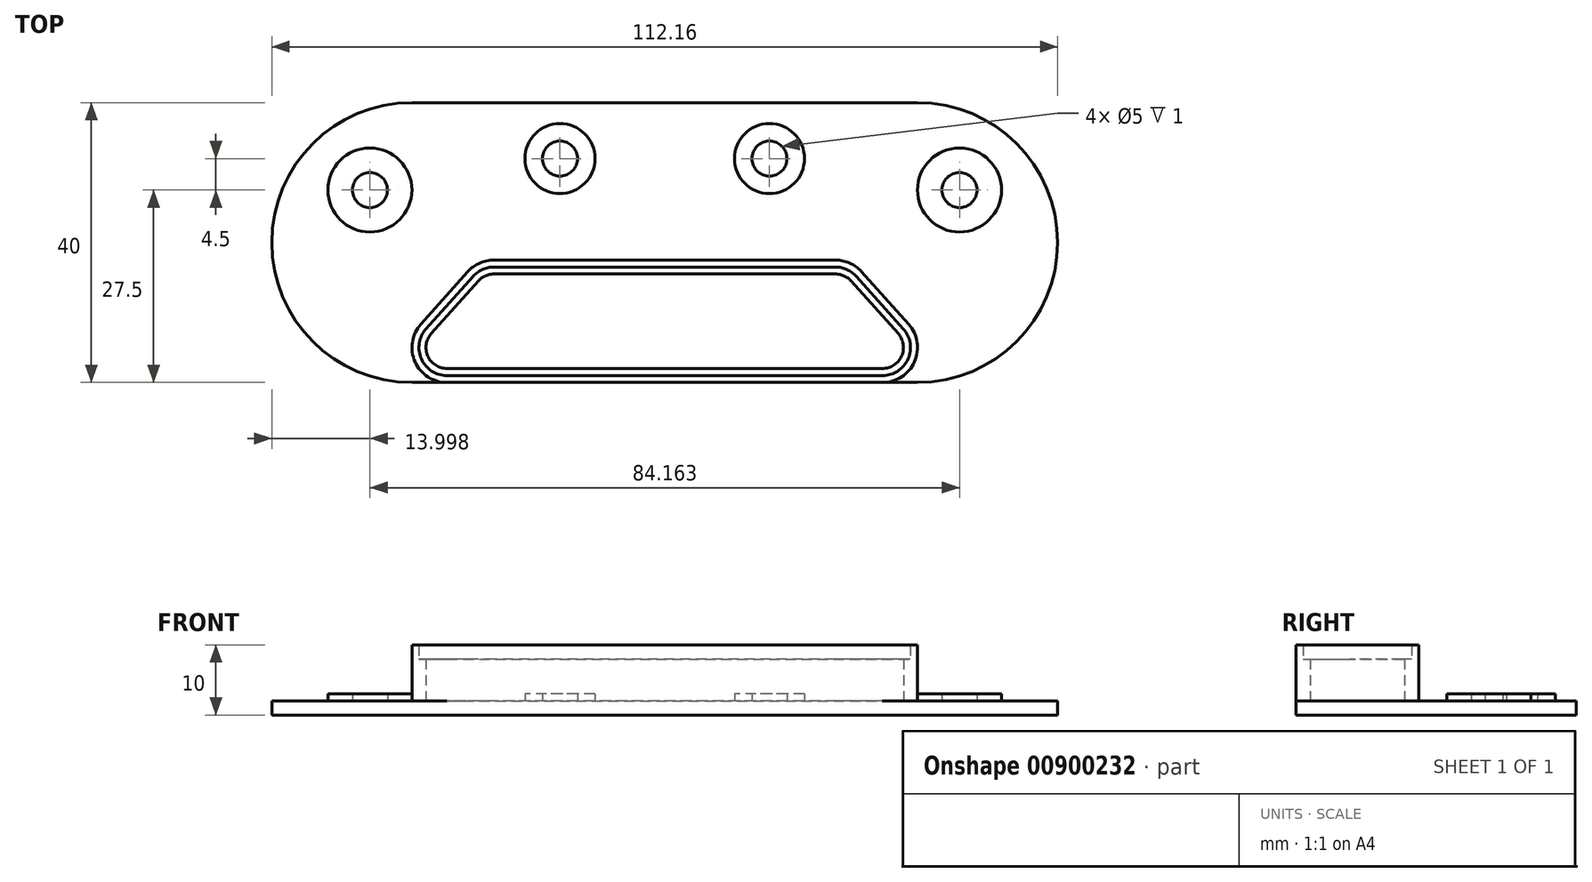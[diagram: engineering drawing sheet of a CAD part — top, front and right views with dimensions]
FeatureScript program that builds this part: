
annotation { "Feature Type Name" : "Feature", "Feature Type Description" : "" }
export const myFeature = defineFeature(function(context is Context, id is Id, definition is map)
    precondition{}
    {
        {
            var Q0;
            Q0=qCreatedBy(makeId("Top.planeOp"),FACE);
            var sketch = newSketch(context, id + "F0", { "sketchPlane" : qUnion([Q0])});
            skLineSegment(sketch, "E0.bottom", {"start": v(36.08, -20) * mm, "end": v(-36.08, -20) * mm});
            skLineSegment(sketch, "E0.top", {"start": v(36.08, 20) * mm, "end": v(-36.08, 20) * mm});
            skLineSegment(sketch, "E0.left", {"start": v(56.08, 0) * mm, "end": v(56.08, 0) * mm});
            skLineSegment(sketch, "E0.right", {"start": v(-56.08, 0) * mm, "end": v(-56.08, 0) * mm});
            skPoint(sketch, "E0.middle", {"position": v(0, 0) * mm});
            skPoint(sketch, "E1.visualSharp", {"position": v(-56.08, -20) * mm});
            skArc(sketch, "E1.filletArc", {"start": v(-56.08, 0) * mm, "mid": v(-50.22, -14.14) * mm, "end": v(-36.08, -20) * mm});
            skPoint(sketch, "E2.visualSharp", {"position": v(-56.08, 20) * mm});
            skArc(sketch, "E2.filletArc", {"start": v(-36.08, 20) * mm, "mid": v(-50.22, 14.14) * mm, "end": v(-56.08, 0) * mm});
            skPoint(sketch, "E3.visualSharp", {"position": v(56.08, 20) * mm});
            skArc(sketch, "E3.filletArc", {"start": v(56.08, 0) * mm, "mid": v(50.22, 14.14) * mm, "end": v(36.08, 20) * mm});
            skPoint(sketch, "E4.visualSharp", {"position": v(56.08, -20) * mm});
            skArc(sketch, "E4.filletArc", {"start": v(36.08, -20) * mm, "mid": v(50.22, -14.14) * mm, "end": v(56.08, 0) * mm});
            skSolve(sketch);
        }
        {
            var Q0;
            Q0 = qSketchRegion(id + "F0", true);
            extrude(context, id + "F1", {"entities" : qUnion([Q0]), "depth" : 2 * mm, "offsetDistance" : 25 * mm});
        }
        {
            var Q0;
            Q0=makeQuery(id+"F1.opExtrude","CAP_FACE",FACE,{"disambiguationData":[OSD([sQuery(id+"F0.wireOp",EDGE,"E0.bottom"),sQuery(id+"F0.wireOp",EDGE,"E0.top"),sQuery(id+"F0.wireOp",EDGE,"E1.filletArc"),sQuery(id+"F0.wireOp",EDGE,"E2.filletArc"),sQuery(id+"F0.wireOp",EDGE,"E3.filletArc"),sQuery(id+"F0.wireOp",EDGE,"E4.filletArc")])],"isStart":false});
            var sketch = newSketch(context, id + "F2", { "sketchPlane" : qUnion([Q0])});
            skLineSegment(sketch, "E5", {"start": v(-76.8, 0) * mm, "end": v(76.55, 0) * mm, "construction": true});
            skLineSegment(sketch, "E6", {"start": v(0, -28.1) * mm, "end": v(0, 41.06) * mm, "construction": true});
            skPoint(sketch, "E6.endSnap0", {"position": v(0, 20) * mm});
            skCircle(sketch, "E7", {"center": v(-42.08, 7.5) * mm, "radius": 6 * mm});
            skCircle(sketch, "E8", {"center": v(-42.08, 7.5) * mm, "radius": 2.5 * mm});
            skCircle(sketch, "E9", {"center": v(-14.95, 12) * mm, "radius": 5 * mm});
            skCircle(sketch, "E10", {"center": v(-14.95, 12) * mm, "radius": 2.5 * mm});
            skCircle(sketch, "E11.MirrorC", {"center": v(42.08, 7.5) * mm, "radius": 2.5 * mm});
            skCircle(sketch, "E12.MirrorC", {"center": v(42.08, 7.5) * mm, "radius": 6 * mm});
            skCircle(sketch, "E13.MirrorC", {"center": v(14.95, 12) * mm, "radius": 5 * mm});
            skCircle(sketch, "E14.MirrorC", {"center": v(14.95, 12) * mm, "radius": 2.5 * mm});
            skSolve(sketch);
        }
        {
            var Q0;
            Q0 = qSketchRegion(id + "F2", true);
            extrude(context, id + "F3", {"entities" : qUnion([Q0]), "operationType" : NewBodyOperationType.ADD, "depth" : 1 * mm, "offsetDistance" : 25 * mm});
        }
        {
            var Q0;
            {var subQ0=sQuery(id+"F0.wireOp",EDGE,"E2.filletArc");var subQ1=sQuery(id+"F0.wireOp",EDGE,"E1.filletArc");var subQ2=sQuery(id+"F0.wireOp",EDGE,"E0.top");var subQ3=sQuery(id+"F0.wireOp",EDGE,"E4.filletArc");var subQ4=sQuery(id+"F0.wireOp",EDGE,"E3.filletArc");var subQ5=sQuery(id+"F0.wireOp",EDGE,"E0.bottom");Q0=makeQuery(id+"F3.boolean.opBoolean","SPLIT",FACE,{"disambiguationData":[TD([makeQuery(id+"F1.opExtrude","SWEPT_FACE",FACE,{"disambiguationData":[OSD([subQ5])]})])],"derivedFrom":makeQuery(id+"F1.opExtrude","CAP_FACE",FACE,{"disambiguationData":[OSD([subQ5,subQ2,subQ1,subQ0,subQ4,subQ3])],"isStart":false})});}
            var sketch = newSketch(context, id + "F4", { "sketchPlane" : qUnion([Q0])});
            skLineSegment(sketch, "E15", {"start": v(0, 31.88) * mm, "end": v(0, -36.97) * mm, "construction": true});
            skLineSegment(sketch, "E16", {"start": v(0, -20) * mm, "end": v(-31.08, -20) * mm});
            skLineSegment(sketch, "E17", {"start": v(-34.8, -11.67) * mm, "end": v(-28.1, -4.17) * mm});
            skLineSegment(sketch, "E18", {"start": v(-24.38, -2.5) * mm, "end": v(0, -2.5) * mm});
            skPoint(sketch, "E19.visualSharp", {"position": v(-42.26, -20) * mm});
            skArc(sketch, "E19.filletArc", {"start": v(-34.8, -11.67) * mm, "mid": v(-35.65, -17.04) * mm, "end": v(-31.08, -20) * mm});
            skPoint(sketch, "E20.visualSharp", {"position": v(-26.61, -2.5) * mm});
            skArc(sketch, "E20.filletArc", {"start": v(-24.38, -2.5) * mm, "mid": v(-26.42, -2.94) * mm, "end": v(-28.1, -4.17) * mm});
            skLineSegment(sketch, "E21.0", {"start": v(0, -19) * mm, "end": v(-31.08, -19) * mm});
            skLineSegment(sketch, "E21.1", {"start": v(-24.38, -3.5) * mm, "end": v(0, -3.5) * mm});
            skArc(sketch, "E21.2", {"start": v(-24.38, -3.5) * mm, "mid": v(-26, -3.85) * mm, "end": v(-27.36, -4.83) * mm});
            skLineSegment(sketch, "E21.3", {"start": v(-34.06, -12.33) * mm, "end": v(-27.36, -4.83) * mm});
            skArc(sketch, "E21.4", {"start": v(-34.06, -12.33) * mm, "mid": v(-34.73, -16.63) * mm, "end": v(-31.08, -19) * mm});
            skPoint(sketch, "E22.MirrorP", {"position": v(26.61, -2.5) * mm});
            skLineSegment(sketch, "E23.MirrorCS", {"start": v(0, -19) * mm, "end": v(31.08, -19) * mm});
            skArc(sketch, "E24.MirrorCS", {"start": v(24.38, -2.5) * mm, "mid": v(26.42, -2.94) * mm, "end": v(28.1, -4.17) * mm});
            skArc(sketch, "E25.MirrorCS", {"start": v(34.06, -12.33) * mm, "mid": v(34.73, -16.63) * mm, "end": v(31.08, -19) * mm});
            skLineSegment(sketch, "E26.MirrorCS", {"start": v(34.06, -12.33) * mm, "end": v(27.36, -4.83) * mm});
            skLineSegment(sketch, "E27.MirrorCS", {"start": v(24.38, -3.5) * mm, "end": v(0, -3.5) * mm});
            skLineSegment(sketch, "E28.MirrorCS", {"start": v(24.38, -2.5) * mm, "end": v(0, -2.5) * mm});
            skArc(sketch, "E29.MirrorCS", {"start": v(24.38, -3.5) * mm, "mid": v(26, -3.85) * mm, "end": v(27.36, -4.83) * mm});
            skLineSegment(sketch, "E30.MirrorCS", {"start": v(0, -20) * mm, "end": v(31.08, -20) * mm});
            skLineSegment(sketch, "E31.MirrorCS", {"start": v(34.8, -11.67) * mm, "end": v(28.1, -4.17) * mm});
            skArc(sketch, "E32.MirrorCS", {"start": v(34.8, -11.67) * mm, "mid": v(35.65, -17.04) * mm, "end": v(31.08, -20) * mm});
            skSolve(sketch);
        }
        {
            var Q0;
            Q0 = qSketchRegion(id + "F4", true);
            extrude(context, id + "F5", {"entities" : qUnion([Q0]), "operationType" : NewBodyOperationType.ADD, "depth" : 8 * mm, "offsetDistance" : 25 * mm});
        }
        {
            var Q0;
            {var subQ3=sQuery(id+"F0.wireOp",EDGE,"E2.filletArc");var subQ4=sQuery(id+"F0.wireOp",EDGE,"E1.filletArc");var subQ6=sQuery(id+"F0.wireOp",EDGE,"E0.bottom");var subQ7=makeQuery(id+"F1.opExtrude","SWEPT_FACE",FACE,{"disambiguationData":[OSD([subQ6])]});var subQ9=sQuery(id+"F0.wireOp",EDGE,"E4.filletArc");var subQ10=sQuery(id+"F0.wireOp",EDGE,"E3.filletArc");var subQ12=sQuery(id+"F0.wireOp",EDGE,"E0.top");Q0=makeQuery(id+"F5.boolean.opBoolean","SPLIT",FACE,{"disambiguationData":[TD([subQ7])],"derivedFrom":makeQuery(id+"F3.boolean.opBoolean","SPLIT",FACE,{"disambiguationData":[TD([subQ7])],"derivedFrom":makeQuery(id+"F1.opExtrude","CAP_FACE",FACE,{"disambiguationData":[OSD([subQ6,subQ12,subQ4,subQ3,subQ10,subQ9])],"isStart":false})})});}
            var sketch = newSketch(context, id + "F6", { "sketchPlane" : qUnion([Q0])});
            skArc(sketch, "E33.0.0", {"start": v(-24.38, -3.5) * mm, "mid": v(-26, -3.85) * mm, "end": v(-27.36, -4.83) * mm});
            skLineSegment(sketch, "E33.0.1", {"start": v(-27.36, -4.83) * mm, "end": v(-34.06, -12.33) * mm});
            skArc(sketch, "E33.0.2", {"start": v(-34.06, -12.33) * mm, "mid": v(-34.73, -16.63) * mm, "end": v(-31.08, -19) * mm});
            skLineSegment(sketch, "E33.0.3", {"start": v(-31.08, -19) * mm, "end": v(31.08, -19) * mm});
            skArc(sketch, "E33.0.4", {"start": v(31.08, -19) * mm, "mid": v(34.73, -16.63) * mm, "end": v(34.06, -12.33) * mm});
            skLineSegment(sketch, "E33.0.5", {"start": v(34.06, -12.33) * mm, "end": v(27.36, -4.83) * mm});
            skArc(sketch, "E33.0.6", {"start": v(27.36, -4.83) * mm, "mid": v(26, -3.85) * mm, "end": v(24.38, -3.5) * mm});
            skLineSegment(sketch, "E33.0.7", {"start": v(24.38, -3.5) * mm, "end": v(-24.38, -3.5) * mm});
            skArc(sketch, "E34.0", {"start": v(26.61, -5.5) * mm, "mid": v(25.6, -4.76) * mm, "end": v(24.38, -4.5) * mm});
            skLineSegment(sketch, "E34.1", {"start": v(33.32, -13) * mm, "end": v(26.61, -5.5) * mm});
            skLineSegment(sketch, "E34.2", {"start": v(24.38, -4.5) * mm, "end": v(-24.38, -4.5) * mm});
            skArc(sketch, "E34.3", {"start": v(31.08, -18) * mm, "mid": v(33.82, -16.22) * mm, "end": v(33.32, -13) * mm});
            skArc(sketch, "E34.4", {"start": v(-24.38, -4.5) * mm, "mid": v(-25.6, -4.76) * mm, "end": v(-26.61, -5.5) * mm});
            skLineSegment(sketch, "E34.5", {"start": v(-26.61, -5.5) * mm, "end": v(-33.32, -13) * mm});
            skArc(sketch, "E34.6", {"start": v(-33.32, -13) * mm, "mid": v(-33.82, -16.22) * mm, "end": v(-31.08, -18) * mm});
            skLineSegment(sketch, "E34.7", {"start": v(-31.08, -18) * mm, "end": v(31.08, -18) * mm});
            skSolve(sketch);
        }
        {
            var Q0;
            Q0 = qSketchRegion(id + "F6", true);
            extrude(context, id + "F7", {"entities" : qUnion([Q0]), "operationType" : NewBodyOperationType.ADD, "depth" : 6 * mm, "offsetDistance" : 25 * mm});
        }
    });
